# Revit family: KDW030052
name_source: partatom
category: Appareils sanitaires
revit_build: Autodesk Revit Architecture 2015 (Build: 20140223_1515(x64)
units: mm (PartAtom-declared; Revit-internal decimal feet)

## types (1)
- KDW030052
    Auteur = Polantis
    Caractéristiques = https://
    Couleur = https://www.kaldewei.co.uk
    Dimension des raccordement = EN 14688
    Durabilité = https://EN 14688
    Finition = https://n
    Forme = Countertop, Double washbasin
    HasGrabHandles = https://
    IfcExportAs = WASHHANDBASIN
    IfcExportType = IfcSanitaryTerminalType
    Information produit = Model No. 3168: The perfect design of a wash area in large bathrooms: modern, spacious, minimalist. Different tap-fitting holes allow the user to choose between use by one or two people.
    IntegralAccessories = https://
    Isolation sonore = DIN 4109:2016, VDI4100:2012
    Lien URL Fabricant = https://www.kaldewei.com
    Lien URL donnée technique = https://
    Lien URL objet = https://
    Matériau = steel enamel
    Nom = PURO AUFSATZ-DOPPELWASCHTISCH
    Nom fabricant = KALDEWEI
    Nom objet = PURO Countertop double washbasin 460x1200
    NominalDepth = 120
    NominalHeight = 120 mm
    NominalLength = 1200
    NominalWidth = 460
    Numéro de série = 3168
    ObjectNorm = EN 14688 EU DECLARATION OF PERFORMANCE (https://www.kaldewei.de
    Options couleurs = https://www.kaldewei.co.uk
    Pays fabricant = GERMANY
    Photo objet = https://
    Poids = 22.8
    Polantis code = KDW030052
    Polmberie = Chrome
    Résistance = https://EN 15804
    SupportFrame = https://
    Taille = 460x1200
    UNSPSCCode = 30181504
    UNSPSCNames = Sinks
    Uniclass2 = Pr_40_20_96
    Version = 3
    WarrantyDurationParts = 30
    WarrantyDurationUnit = Year
    WarrantyStartDate = https://www.kaldewei.co.uk

## geometry (parser evidence)
native form markers: Sweep x6
no freeform markers — native parametric forms only
